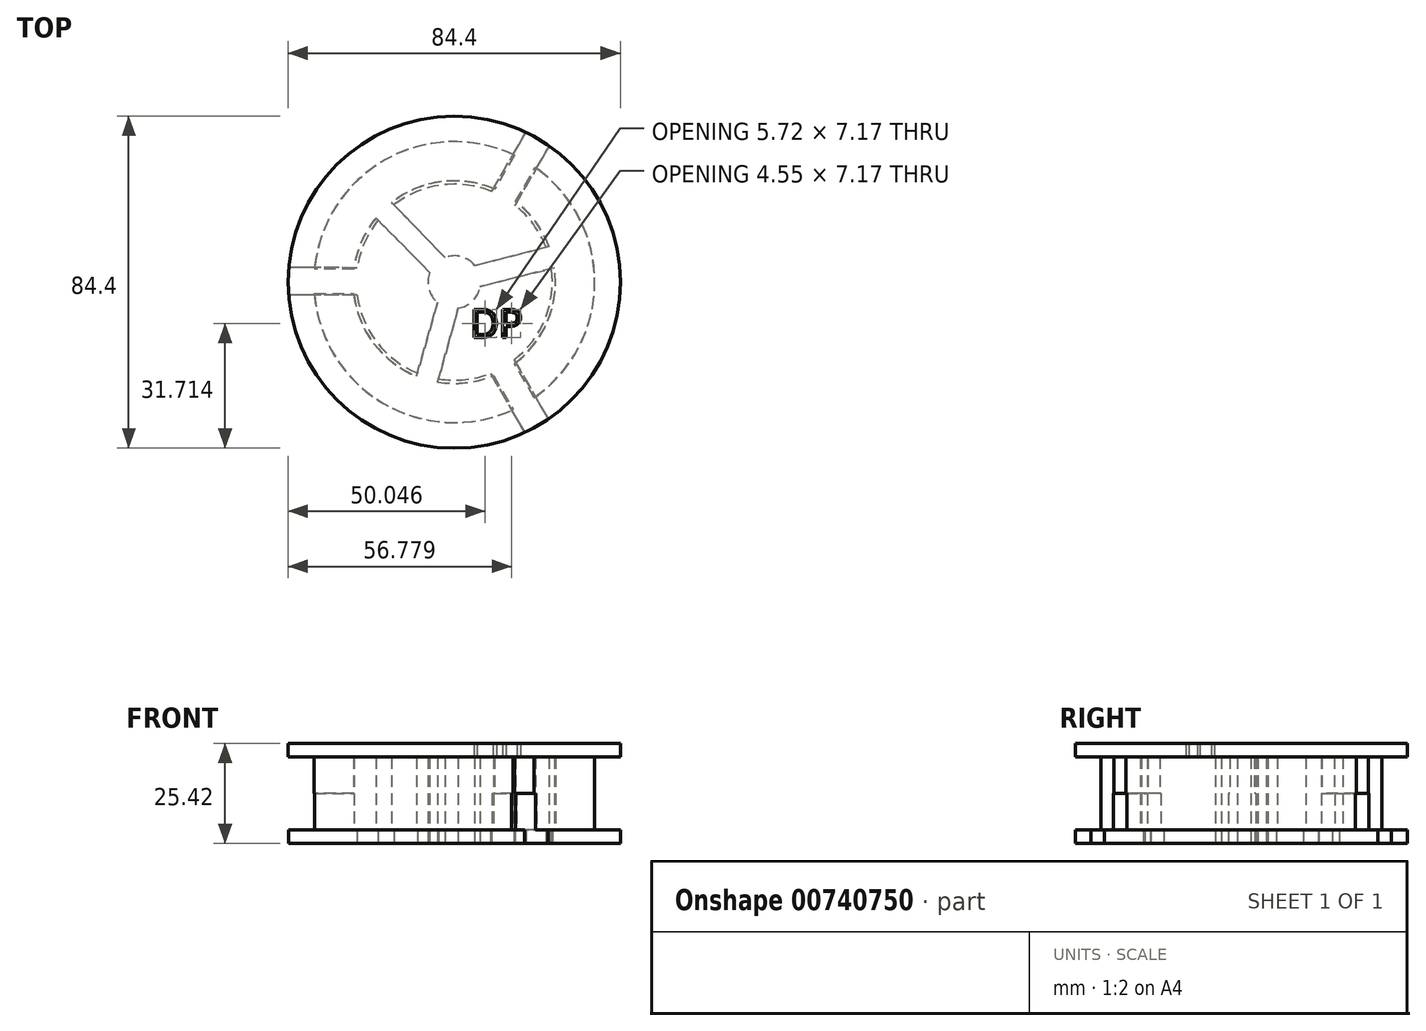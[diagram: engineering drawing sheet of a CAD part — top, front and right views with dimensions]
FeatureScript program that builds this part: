
annotation { "Feature Type Name" : "Feature", "Feature Type Description" : "" }
export const myFeature = defineFeature(function(context is Context, id is Id, definition is map)
    precondition{}
    {
        {
            var Q0;
            Q0=qCreatedBy(makeId("Top.planeOp"),FACE);
            var sketch = newSketch(context, id + "F0", { "sketchPlane" : qUnion([Q0])});
            skCircle(sketch, "E0", {"center": v(0, 0) * mm, "radius": 35.68 * mm});
            skCircle(sketch, "E1", {"center": v(0, 0) * mm, "radius": 25.72 * mm});
            skLineSegment(sketch, "E2", {"start": v(-35.53, 3.26) * mm, "end": v(-25.51, 3.26) * mm});
            skLineSegment(sketch, "E3", {"start": v(-25.56, -2.92) * mm, "end": v(-35.56, -2.92) * mm});
            skLineSegment(sketch, "E4.1.0", {"start": v(14.94, -32.4) * mm, "end": v(9.93, -23.73) * mm});
            skLineSegment(sketch, "E4.1.1", {"start": v(15.3, -20.67) * mm, "end": v(20.3, -29.34) * mm});
            skLineSegment(sketch, "E4.2.0", {"start": v(20.6, 29.14) * mm, "end": v(15.58, 20.46) * mm});
            skLineSegment(sketch, "E4.2.1", {"start": v(10.25, 23.6) * mm, "end": v(15.25, 32.25) * mm});
            skCircle(sketch, "E5", {"center": v(0, 0) * mm, "radius": 6.7 * mm});
            skLineSegment(sketch, "E6", {"start": v(-6.24, 2.42) * mm, "end": v(-19.88, 16.32) * mm});
            skLineSegment(sketch, "E7", {"start": v(-2.35, 6.27) * mm, "end": v(-15.87, 20.24) * mm});
            skLineSegment(sketch, "E8.1.0", {"start": v(-4.25, -5.17) * mm, "end": v(-9.6, -23.87) * mm});
            skLineSegment(sketch, "E8.1.1", {"start": v(1.03, -6.61) * mm, "end": v(-4.19, -25.38) * mm});
            skLineSegment(sketch, "E8.2.0", {"start": v(6.6, -1.1) * mm, "end": v(25.47, 3.63) * mm});
            skLineSegment(sketch, "E8.2.1", {"start": v(5.21, 4.2) * mm, "end": v(24.07, 9.06) * mm});
            skSolve(sketch);
        }
        {
            var Q0;
            {var subQ4=sQuery(id+"F0.wireOp",EDGE,"E3");Q0=makeQuery(id+"F0.imprint","IMPRINT",FACE,{"disambiguationData":[TD([[makeQuery(id+"F0.imprint","IMPRINT",EDGE,{"derivedFrom":subQ4}),1.0]])]});}
            var Q1;
            {var subQ4=sQuery(id+"F0.wireOp",EDGE,"E2");Q1=makeQuery(id+"F0.imprint","IMPRINT",FACE,{"disambiguationData":[TD([[makeQuery(id+"F0.imprint","IMPRINT",EDGE,{"derivedFrom":subQ4}),1.0]])]});}
            var Q2;
            {var subQ0=sQuery(id+"F0.wireOp",EDGE,"E4.1.1");Q2=makeQuery(id+"F0.imprint","IMPRINT",FACE,{"disambiguationData":[TD([[makeQuery(id+"F0.imprint","IMPRINT",EDGE,{"derivedFrom":subQ0}),1.0]])]});}
            var Q3;
            {var subQ0=sQuery(id+"F0.wireOp",EDGE,"E6");Q3=makeQuery(id+"F0.imprint","IMPRINT",FACE,{"disambiguationData":[TD([[makeQuery(id+"F0.imprint","IMPRINT",EDGE,{"derivedFrom":subQ0}),-1.0]])]});}
            var Q4;
            {var subQ0=sQuery(id+"F0.wireOp",EDGE,"E8.2.0");Q4=makeQuery(id+"F0.imprint","IMPRINT",FACE,{"disambiguationData":[TD([[makeQuery(id+"F0.imprint","IMPRINT",EDGE,{"derivedFrom":subQ0}),1.0]])]});}
            var Q5;
            {var subQ0=sQuery(id+"F0.wireOp",EDGE,"E8.1.0");Q5=makeQuery(id+"F0.imprint","IMPRINT",FACE,{"disambiguationData":[TD([[makeQuery(id+"F0.imprint","IMPRINT",EDGE,{"derivedFrom":subQ0}),1.0]])]});}
            var Q6;
            {var subQ0=sQuery(id+"F0.wireOp",EDGE,"E5");var subQ4=makeQuery(id+"F0.imprint","INTERSECT",VERTEX,{"derivedFrom":[subQ0,sQuery(id+"F0.wireOp",EDGE,"E7")]});Q6=makeQuery(id+"F0.imprint","IMPRINT",FACE,{"disambiguationData":[TD([[makeQuery(id+"F0.imprint","IMPRINT",EDGE,{"disambiguationData":[TD([[subQ4,1.0]])],"derivedFrom":subQ0}),1.0]])]});}
            extrude(context, id + "F1", {"entities" : qUnion([Q0, Q1, Q2, Q3, Q4, Q5, Q6]), "depth" : 25.4 * mm, "offsetDistance" : 25.4 * mm});
        }
        {
            var Q0;
            Q0=qCreatedBy(makeId("Front.planeOp"),FACE);
            var sketch = newSketch(context, id + "F2", { "sketchPlane" : qUnion([Q0])});
            skLineSegment(sketch, "E9.bottom", {"start": v(0, 0) * mm, "end": v(-42.2, 0) * mm});
            skLineSegment(sketch, "E9.top", {"start": v(0, 3.48) * mm, "end": v(-42.2, 3.48) * mm});
            skLineSegment(sketch, "E9.left", {"start": v(0, 0) * mm, "end": v(0, 3.48) * mm});
            skLineSegment(sketch, "E9.right", {"start": v(-42.2, 0) * mm, "end": v(-42.2, 3.48) * mm});
            skLineSegment(sketch, "E10", {"start": v(0, 12.71) * mm, "end": v(-57.43, 12.71) * mm, "construction": true});
            skLineSegment(sketch, "E11.MirrorCS", {"start": v(0, 21.94) * mm, "end": v(-42.2, 21.94) * mm});
            skLineSegment(sketch, "E12.MirrorCS", {"start": v(-42.2, 25.42) * mm, "end": v(-42.2, 21.94) * mm});
            skLineSegment(sketch, "E13.MirrorCS", {"start": v(0, 25.42) * mm, "end": v(-42.2, 25.42) * mm});
            skLineSegment(sketch, "E14.MirrorCS", {"start": v(0, 25.42) * mm, "end": v(0, 21.94) * mm});
            skLineSegment(sketch, "E15", {"start": v(0, 0) * mm, "end": v(0, 37.81) * mm});
            skLineSegment(sketch, "E16", {"start": v(-24.9, 21.94) * mm, "end": v(-24.9, 0) * mm});
            skSolve(sketch);
        }
        {
            var Q0;
            {var subQ0=sQuery(id+"F2.wireOp",EDGE,"E12.MirrorCS");Q0=makeQuery(id+"F2.imprint","IMPRINT",FACE,{"disambiguationData":[TD([[makeQuery(id+"F2.imprint","IMPRINT",EDGE,{"derivedFrom":subQ0}),1.0]])]});}
            var Q1;
            {var subQ0=sQuery(id+"F2.wireOp",EDGE,"E9.right");Q1=makeQuery(id+"F2.imprint","IMPRINT",FACE,{"disambiguationData":[TD([[makeQuery(id+"F2.imprint","IMPRINT",EDGE,{"derivedFrom":subQ0}),-1.0]])]});}
            var Q2;
            Q2=sQuery(id+"F2.wireOp",EDGE,"E15");
            revolve(context, id + "F3", {"operationType" : NewBodyOperationType.ADD, "surfaceOperationType" : NewSurfaceOperationType.NEW, "entities" : qUnion([Q0, Q1]), "axis" : qUnion([Q2]), "revolveType" : RevolveType.FULL});
        }
        {
            var Q0;
            Q0=qCreatedBy(makeId("Top.planeOp"),FACE);
            var sketch = newSketch(context, id + "F4", { "sketchPlane" : qUnion([Q0])});
            skLineSegment(sketch, "E17", {"start": v(-23.1, -3.23) * mm, "end": v(-46.84, -3.23) * mm});
            skLineSegment(sketch, "E18", {"start": v(-22.84, 3.23) * mm, "end": v(-47.62, 3.23) * mm});
            skLineSegment(sketch, "E19.1.0", {"start": v(14.34, -18.4) * mm, "end": v(26.22, -38.96) * mm});
            skLineSegment(sketch, "E19.1.1", {"start": v(8.63, -21.4) * mm, "end": v(21.02, -42.85) * mm});
            skLineSegment(sketch, "E19.2.0", {"start": v(8.76, 21.62) * mm, "end": v(20.63, 42.18) * mm});
            skLineSegment(sketch, "E19.2.1", {"start": v(14.21, 18.17) * mm, "end": v(26.6, 39.63) * mm});
            skPoint(sketch, "E19.center", {"position": v(0, 0) * mm});
            skLineSegment(sketch, "E20", {"start": v(-47.62, 3.23) * mm, "end": v(-46.84, -3.23) * mm});
            skLineSegment(sketch, "E21", {"start": v(-22.84, 3.23) * mm, "end": v(-23.1, -3.23) * mm});
            skLineSegment(sketch, "E22.1.0", {"start": v(21.02, -42.85) * mm, "end": v(26.22, -38.96) * mm});
            skLineSegment(sketch, "E22.1.1", {"start": v(8.63, -21.4) * mm, "end": v(14.34, -18.4) * mm});
            skLineSegment(sketch, "E22.2.0", {"start": v(26.6, 39.63) * mm, "end": v(20.63, 42.18) * mm});
            skLineSegment(sketch, "E22.2.1", {"start": v(14.21, 18.17) * mm, "end": v(8.76, 21.62) * mm});
            skSolve(sketch);
        }
        {
            var Q0;
            Q0 = qSketchRegion(id + "F4", true);
            extrude(context, id + "F5", {"entities" : qUnion([Q0]), "operationType" : NewBodyOperationType.REMOVE, "oppositeDirection" : true, "depth" : 5.08 * mm, "offsetDistance" : 25.4 * mm});
        }
        {
            var Q0;
            Q0=qCreatedBy(makeId("Top.planeOp"),FACE);
            cPlane(context, id + "F6", {"entities" : qUnion([Q0]), "cplaneType" : CPlaneType.OFFSET, "offset" : 21.84 * mm, "width" : 152.4 * mm, "height" : 152.4 * mm});
        }
        {
            var Q0;
            Q0=qCreatedBy(id+"F6.planeOp",FACE);
            var sketch = newSketch(context, id + "F7", { "sketchPlane" : qUnion([Q0])});
            skText(sketch, "E23", { "text": "DP", "fontName": "OpenSans-Regular.ttf"});
            const initialGuessF7  = {"E23": [0.004, -0.01407, 1, 0, 0.00723]};
            skSetInitialGuess(sketch, initialGuessF7);
            skSolve(sketch);
        }
        {
            var Q0;
            Q0 = qSketchRegion(id + "F7", true);
            extrude(context, id + "F8", {"entities" : qUnion([Q0]), "operationType" : NewBodyOperationType.REMOVE, "depth" : 25.4 * mm, "offsetDistance" : 25.4 * mm});
        }
        {
            var Q0;
            Q0=qCreatedBy(makeId("Top.planeOp"),FACE);
            var sketch = newSketch(context, id + "F9", { "sketchPlane" : qUnion([Q0])});
            skLineSegment(sketch, "E24", {"start": v(8.39, -21.8) * mm, "end": v(23.87, -48.65) * mm});
            skLineSegment(sketch, "E25", {"start": v(14.58, -18.71) * mm, "end": v(31.87, -48.65) * mm});
            skLineSegment(sketch, "E26", {"start": v(31.87, -48.65) * mm, "end": v(23.87, -48.65) * mm});
            skLineSegment(sketch, "E27", {"start": v(8.39, -21.8) * mm, "end": v(14.58, -18.71) * mm});
            skLineSegment(sketch, "E28.1.0", {"start": v(14.7, 18.17) * mm, "end": v(8.91, 21.98) * mm});
            skLineSegment(sketch, "E28.1.1", {"start": v(14.7, 18.17) * mm, "end": v(30.2, 45) * mm});
            skLineSegment(sketch, "E28.1.2", {"start": v(26.2, 51.93) * mm, "end": v(30.2, 45) * mm});
            skLineSegment(sketch, "E28.1.3", {"start": v(8.91, 21.98) * mm, "end": v(26.2, 51.93) * mm});
            skLineSegment(sketch, "E28.2.0", {"start": v(-23.08, 3.64) * mm, "end": v(-23.5, -3.27) * mm});
            skLineSegment(sketch, "E28.2.1", {"start": v(-23.08, 3.64) * mm, "end": v(-54.07, 3.65) * mm});
            skLineSegment(sketch, "E28.2.2", {"start": v(-58.07, -3.28) * mm, "end": v(-54.07, 3.65) * mm});
            skLineSegment(sketch, "E28.2.3", {"start": v(-23.5, -3.27) * mm, "end": v(-58.07, -3.28) * mm});
            skPoint(sketch, "E28.center", {"position": v(0, 0) * mm});
            skSolve(sketch);
        }
        {
            var Q0;
            Q0 = qSketchRegion(id + "F9", true);
            extrude(context, id + "F10", {"entities" : qUnion([Q0]), "operationType" : NewBodyOperationType.REMOVE, "depth" : 12.7 * mm, "offsetDistance" : 25.4 * mm});
        }
    });
